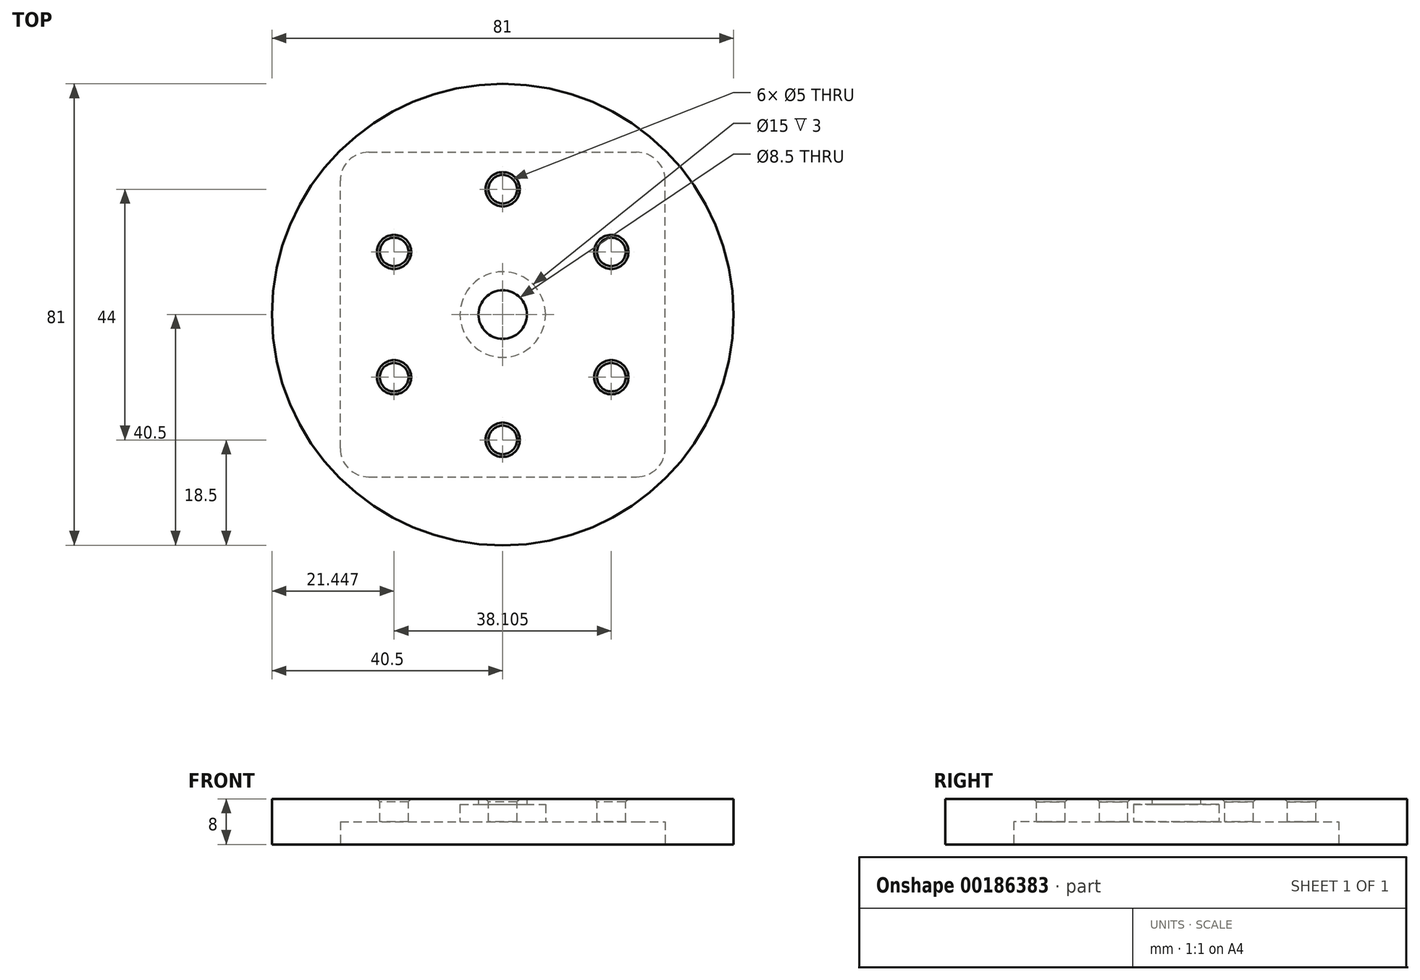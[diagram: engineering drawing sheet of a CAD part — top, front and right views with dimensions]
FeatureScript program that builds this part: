
annotation { "Feature Type Name" : "Feature", "Feature Type Description" : "" }
export const myFeature = defineFeature(function(context is Context, id is Id, definition is map)
    precondition{}
    {
        {
            var Q0;
            Q0=qCreatedBy(makeId("Top.planeOp"),FACE);
            var sketch = newSketch(context, id + "F0", { "sketchPlane" : qUnion([Q0])});
            skCircle(sketch, "E0", {"center": v(0, 0) * mm, "radius": 40.5 * mm});
            skSolve(sketch);
        }
        {
            var Q0;
            Q0=makeQuery(id+"F0.imprint","IMPRINT",FACE,{"disambiguationData":[TD([[makeQuery(id+"F0.imprint","IMPRINT",EDGE,{"derivedFrom":sQuery(id+"F0.wireOp",EDGE,"E0")}),1.0]])]});
            extrude(context, id + "F1", {"entities" : qUnion([Q0]), "depth" : 8 * mm});
        }
        {
            var Q0;
            Q0=makeQuery(id+"F1.opExtrude","CAP_FACE",FACE,{"disambiguationData":[OSD([sQuery(id+"F0.wireOp",EDGE,"E0")])],"isStart":false});
            var sketch = newSketch(context, id + "F2", { "sketchPlane" : qUnion([Q0])});
            skPoint(sketch, "E1", {"position": v(0, 22) * mm});
            skLineSegment(sketch, "E2", {"start": v(0, 0) * mm, "end": v(0, 40.5) * mm, "construction": true});
            skPoint(sketch, "E3.1.0", {"position": v(19.05, 11) * mm});
            skPoint(sketch, "E3.2.0", {"position": v(19.05, -11) * mm});
            skPoint(sketch, "E3.3.0", {"position": v(0, -22) * mm});
            skPoint(sketch, "E3.4.0", {"position": v(-19.05, -11) * mm});
            skPoint(sketch, "E3.5.0", {"position": v(-19.05, 11) * mm});
            skPoint(sketch, "E3.center", {"position": v(0, 0) * mm});
            skLineSegment(sketch, "E3.anchor1", {"start": v(0, 0) * mm, "end": v(0, 22) * mm, "construction": true});
            skLineSegment(sketch, "E3.anchor2", {"start": v(0, 0) * mm, "end": v(-19.05, 11) * mm, "construction": true});
            skSolve(sketch);
        }
        {
            var Q0;
            Q0=sQuery(id+"F2.wireOp",VERTEX,"E1");
            var Q1;
            Q1=sQuery(id+"F2.wireOp",VERTEX,"68f1edd6-98f7-46e9-8584-7c4fae7190c2.1.0");
            var Q2;
            Q2=sQuery(id+"F2.wireOp",VERTEX,"68f1edd6-98f7-46e9-8584-7c4fae7190c2.2.0");
            var Q3;
            Q3=sQuery(id+"F2.wireOp",VERTEX,"E3.1.0");
            var Q4;
            Q4=sQuery(id+"F2.wireOp",VERTEX,"E3.2.0");
            var Q5;
            Q5=sQuery(id+"F2.wireOp",VERTEX,"E3.3.0");
            var Q6;
            Q6=sQuery(id+"F2.wireOp",VERTEX,"E3.4.0");
            var Q7;
            Q7=sQuery(id+"F2.wireOp",VERTEX,"E3.5.0");
            var Q8;
            Q8=makeQuery(id+"F1.opExtrude","SWEPT_BODY",BODY,{"disambiguationData":[OSD([sQuery(id+"F0.wireOp",EDGE,"E0")])]});
            hole(context, id + "F3", {"style" : HoleStyle.C_SINK, "endStyle" : HoleEndStyle.THROUGH, "holeDiameter" : 5 * mm, "cSinkDiameter" : 6 * mm, "cSinkAngle" : 90 * degree, "locations" : qUnion([Q0, Q1, Q2, Q3, Q4, Q5, Q6, Q7]), "scope" : qUnion([Q8]), "tappedDepth" : 12 * mm, "tapClearance" : 3});
        }
        {
            var Q0;
            Q0=makeQuery(id+"F1.opExtrude","CAP_FACE",FACE,{"disambiguationData":[OSD([sQuery(id+"F0.wireOp",EDGE,"E0")])],"isStart":true});
            var sketch = newSketch(context, id + "F4", { "sketchPlane" : qUnion([Q0])});
            skCircle(sketch, "E4", {"center": v(0, 0) * mm, "radius": 7.5 * mm});
            skSolve(sketch);
        }
        {
            var Q0;
            Q0=makeQuery(id+"F4.imprint","IMPRINT",FACE,{"disambiguationData":[TD([[makeQuery(id+"F4.imprint","IMPRINT",EDGE,{"derivedFrom":sQuery(id+"F4.wireOp",EDGE,"E4")}),1.0]])]});
            extrude(context, id + "F5", {"entities" : qUnion([Q0]), "operationType" : NewBodyOperationType.REMOVE, "oppositeDirection" : true, "depth" : 7 * mm});
        }
        {
            var Q0;
            Q0=makeQuery(id+"F5.boolean.opBoolean","COPY",FACE,{"derivedFrom":makeQuery(id+"F5.opExtrude","CAP_FACE",FACE,{"disambiguationData":[OSD([sQuery(id+"F4.wireOp",EDGE,"E4")])],"isStart":false})});
            var sketch = newSketch(context, id + "F6", { "sketchPlane" : qUnion([Q0])});
            skCircle(sketch, "E5", {"center": v(0, 0) * mm, "radius": 4.25 * mm});
            skSolve(sketch);
        }
        {
            var Q0;
            Q0=makeQuery(id+"F6.imprint","IMPRINT",FACE,{"disambiguationData":[TD([[makeQuery(id+"F6.imprint","IMPRINT",EDGE,{"derivedFrom":sQuery(id+"F6.wireOp",EDGE,"E5")}),1.0]])]});
            extrude(context, id + "F7", {"entities" : qUnion([Q0]), "operationType" : NewBodyOperationType.REMOVE, "endBound" : BoundingType.THROUGH_ALL, "oppositeDirection" : true, "depth" : 25 * mm});
        }
        {
            var Q0;
            Q0=makeQuery(id+"F1.opExtrude","CAP_FACE",FACE,{"disambiguationData":[OSD([sQuery(id+"F0.wireOp",EDGE,"E0")])],"isStart":true});
            var sketch = newSketch(context, id + "F8", { "sketchPlane" : qUnion([Q0])});
            skLineSegment(sketch, "E6.bottom", {"start": v(-28.5, 28.5) * mm, "end": v(28.5, 28.5) * mm});
            skLineSegment(sketch, "E6.top", {"start": v(-28.5, -28.5) * mm, "end": v(28.5, -28.5) * mm});
            skLineSegment(sketch, "E6.left", {"start": v(-28.5, 28.5) * mm, "end": v(-28.5, -28.5) * mm});
            skLineSegment(sketch, "E6.right", {"start": v(28.5, 28.5) * mm, "end": v(28.5, -28.5) * mm});
            skPoint(sketch, "E6.middle", {"position": v(0, 0) * mm});
            skSolve(sketch);
        }
        {
            var Q0;
            Q0=makeQuery(id+"F8.imprint","IMPRINT",FACE,{"disambiguationData":[TD([[makeQuery(id+"F8.imprint","IMPRINT",EDGE,{"derivedFrom":sQuery(id+"F8.wireOp",EDGE,"E6.bottom")}),-1.0]])]});
            extrude(context, id + "F9", {"entities" : qUnion([Q0]), "operationType" : NewBodyOperationType.REMOVE, "oppositeDirection" : true, "depth" : 4 * mm});
        }
        {
            var Q0;
            Q0=makeQuery(id+"F9.boolean.opBoolean","COPY",EDGE,{"derivedFrom":makeQuery(id+"F9.opExtrude","SWEPT_EDGE",EDGE,{"disambiguationData":[OSD([sQuery(id+"F8.wireOp",EDGE,"E6.top"),sQuery(id+"F8.wireOp",EDGE,"E6.right")])]})});
            var Q1;
            Q1=makeQuery(id+"F9.boolean.opBoolean","COPY",EDGE,{"derivedFrom":makeQuery(id+"F9.opExtrude","SWEPT_EDGE",EDGE,{"disambiguationData":[OSD([sQuery(id+"F8.wireOp",EDGE,"E6.bottom"),sQuery(id+"F8.wireOp",EDGE,"E6.right")])]})});
            var Q2;
            Q2=makeQuery(id+"F9.boolean.opBoolean","COPY",EDGE,{"derivedFrom":makeQuery(id+"F9.opExtrude","SWEPT_EDGE",EDGE,{"disambiguationData":[OSD([sQuery(id+"F8.wireOp",EDGE,"E6.bottom"),sQuery(id+"F8.wireOp",EDGE,"E6.left")])]})});
            var Q3;
            Q3=makeQuery(id+"F9.boolean.opBoolean","COPY",EDGE,{"derivedFrom":makeQuery(id+"F9.opExtrude","SWEPT_EDGE",EDGE,{"disambiguationData":[OSD([sQuery(id+"F8.wireOp",EDGE,"E6.top"),sQuery(id+"F8.wireOp",EDGE,"E6.left")])]})});
            fillet(context, id + "F10", {"entities" : qUnion([Q0, Q1, Q2, Q3]), "radius" : 5 * mm, "tangentPropagation" : true, "allowEdgeOverflow" : false});
        }
    });
